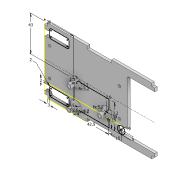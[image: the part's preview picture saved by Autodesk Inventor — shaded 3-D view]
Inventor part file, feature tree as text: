
AUTODESK INVENTOR PART (.ipt)
format: ipt  version: 2022 (Build 260153000, 153)  size: 332,288 bytes
history: native  units: mm
features: extrude x8, sketch x5, fillet x2
ambient origin geometry x8: Origin, YZ Plane, XZ Plane, XY Plane, X Axis, Y Axis, Z Axis, Center Point
bodies: Solid1 (feature_tree)
feature tree (15):
  extrude  "Base Plate"  Depth=80.0mm
  sketch  "Sketch2"  dims[d2=3.5mm d3=3.5mm]
  extrude  "CubePilot Outline"  Depth=3.5mm
  extrude  "Extrusion3"  Depth=3.5mm
  sketch  "Sketch3"  dims[d4=3.5mm d5=3.5mm]
  extrude  "Extrusion4"  Depth=49.0mm
  fillet  "Fillet1"  Radius=3.5mm
  extrude  "Extrusion5"  Depth=3.0mm TaperAngle=0.0deg
  extrude  "Extrusion6"  Depth=44.29mm
  extrude  "Extrusion7"  TaperAngle=0.0deg  [1 undecoded]
  extrude  "Extrusion8"  Depth=94.46mm
  fillet  "Fillet2"  Radius=2.0mm
  sketch  "Sketch1"  dims[d0=134.5mm d1=80.0mm]
  sketch  "Sketch4"  dims[d6=49.0mm d7=49.0mm d8=3.5mm]
  sketch  "Sketch6"  dims[d9=3.5mm d10=3.0mm d11=0.0mm d12=44.29mm d13=0.0mm d14=94.46mm d15=2.0mm d16=4.0mm d17=1.0mm d18=2.8mm d19=20.0mm d21=85.0mm d22=20.0mm d24=34.4mm d27=4.73mm d28=4.945mm d29=0.5mm d30=0.0mm d31=0.0mm d32=0.0mm d33=42.5mm d34=30.0mm d35=43.0mm d36=36.0mm d37=3.2mm d38=3.2mm d39=3.2mm d40=2.5mm d41=2.5mm d42=2.5mm d43=2.5mm d44=2.6mm d45=15.0mm d46=9.0mm d47=5.0mm d48=15.0mm d49=3.0mm d50=4.0mm d51=2.0mm d52=6.0mm d53=2.0mm d54=5.2mm d55=5.2mm d56=5.2mm d57=8.5mm d58=0.0mm d59=4.0mm d60=6.0mm d61=6.0mm d62=6.0mm d63=2.8mm d64=0.0mm d65=0.0mm d66=0.0mm d67=7.5mm d68=7.5mm d69=0.0mm d70=4.0mm d71=2.0mm d72=0.0mm d73=0.0mm d74=12.0mm d75=5.0mm d76=15.0mm d77=15.0mm d78=6.0mm d79=8.0mm d80=2.0mm d81=8.0mm d82=2.0mm d83=0.0mm d84=0.0mm d85=2.0mm]
note: 1 required parameter value undecoded (feature->parameter linkage not recoverable at this tier; creation-order binding heuristic only, values carry confidence <= 0.55)
